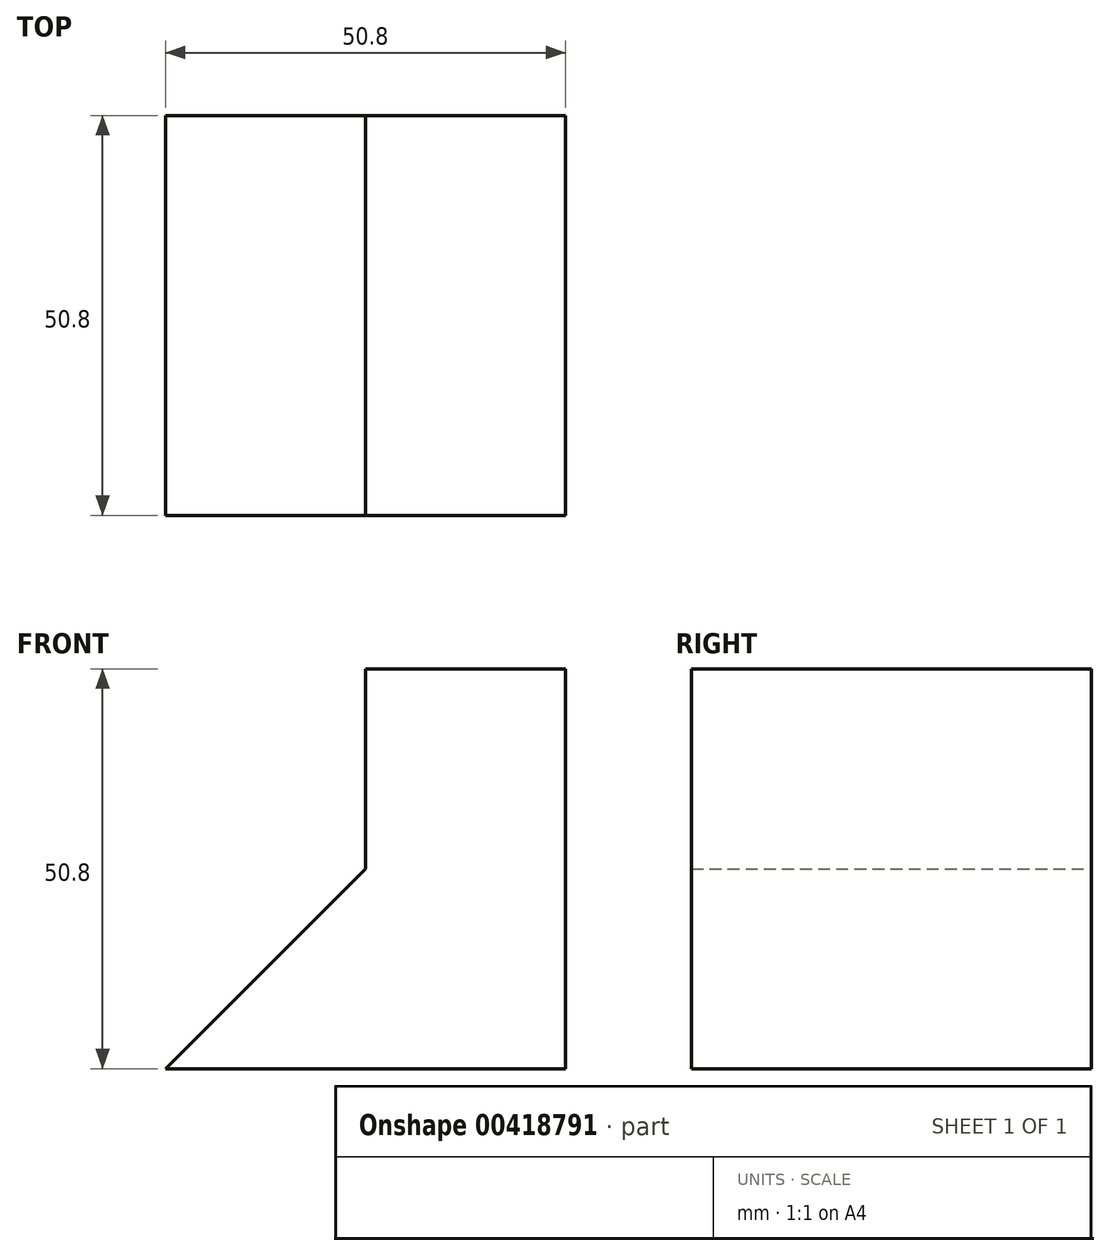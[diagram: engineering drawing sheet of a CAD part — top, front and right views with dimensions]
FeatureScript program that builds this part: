
annotation { "Feature Type Name" : "Feature", "Feature Type Description" : "" }
export const myFeature = defineFeature(function(context is Context, id is Id, definition is map)
    precondition{}
    {
        {
            var Q0;
            Q0=qCreatedBy(makeId("Front.planeOp"),FACE);
            var sketch = newSketch(context, id + "F0", { "sketchPlane" : qUnion([Q0])});
            skLineSegment(sketch, "E0", {"start": v(0, 0) * mm, "end": v(0, 50.8) * mm});
            skLineSegment(sketch, "E1", {"start": v(0, 50.8) * mm, "end": v(-25.4, 50.8) * mm});
            skLineSegment(sketch, "E2", {"start": v(-25.4, 50.8) * mm, "end": v(-25.4, 25.4) * mm});
            skLineSegment(sketch, "E3", {"start": v(0, 0) * mm, "end": v(-50.8, 0) * mm});
            skLineSegment(sketch, "E4", {"start": v(-50.8, 0) * mm, "end": v(-25.4, 25.4) * mm});
            skSolve(sketch);
        }
        {
            var Q0;
            Q0=makeQuery(id+"F0.imprint","IMPRINT",FACE,{"disambiguationData":[TD([[makeQuery(id+"F0.imprint","IMPRINT",EDGE,{"derivedFrom":sQuery(id+"F0.wireOp",EDGE,"E0")}),1.0]])]});
            extrude(context, id + "F1", {"entities" : qUnion([Q0]), "depth" : 50.8 * mm});
        }
    });
